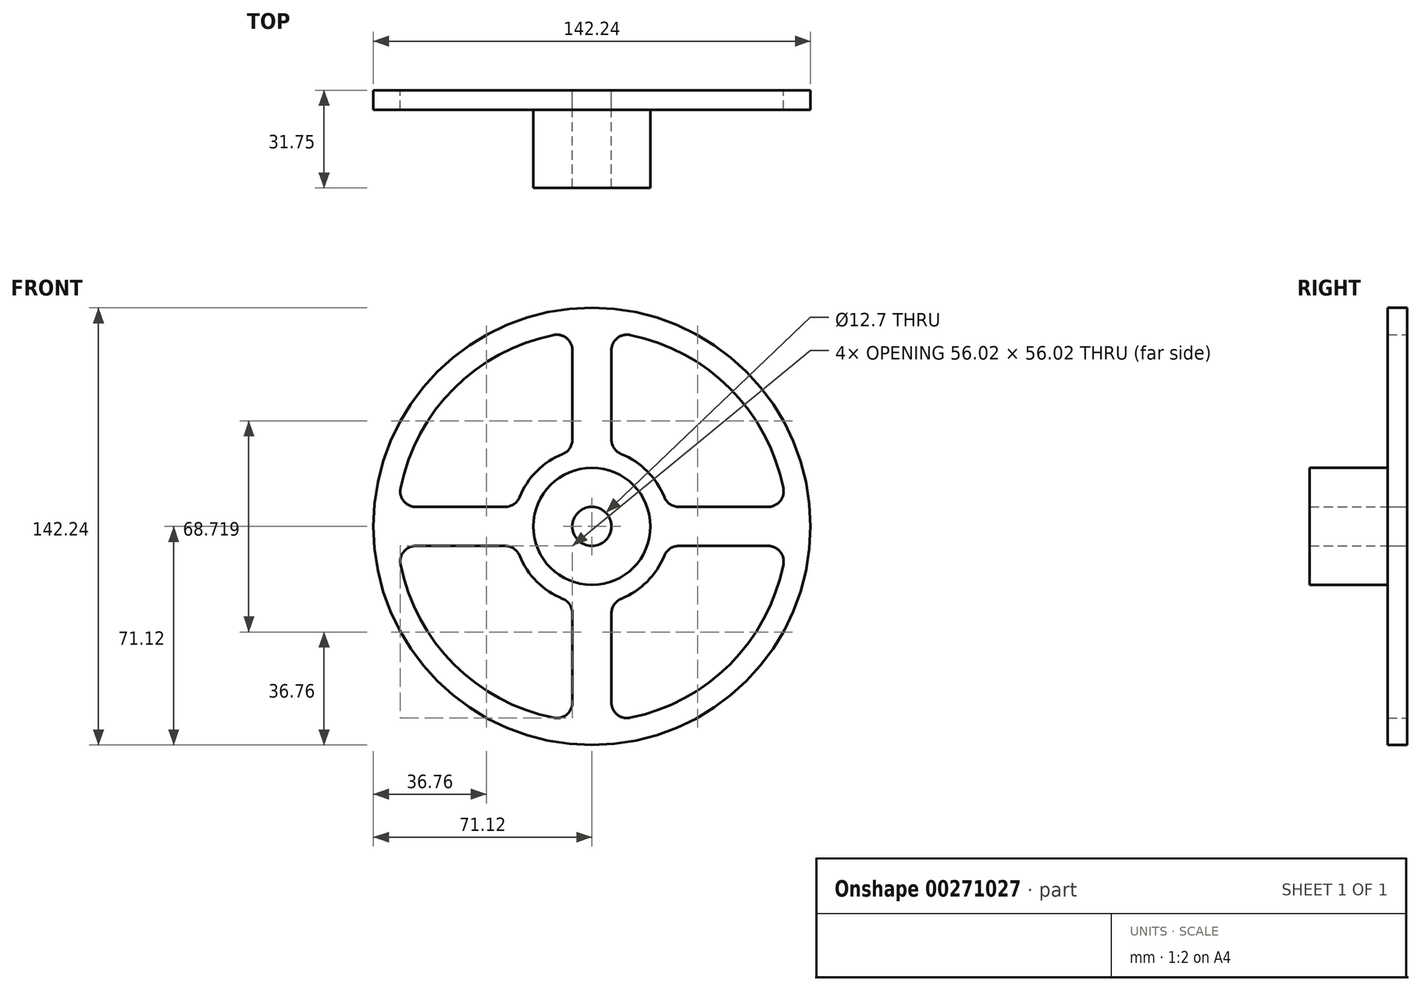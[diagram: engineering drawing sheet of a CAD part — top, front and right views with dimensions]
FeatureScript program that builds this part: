
annotation { "Feature Type Name" : "Feature", "Feature Type Description" : "" }
export const myFeature = defineFeature(function(context is Context, id is Id, definition is map)
    precondition{}
    {
        {
            var Q0;
            Q0=qCreatedBy(makeId("Front.planeOp"),FACE);
            var sketch = newSketch(context, id + "F0", { "sketchPlane" : qUnion([Q0])});
            skCircle(sketch, "E0", {"center": v(0, 0) * mm, "radius": 71.12 * mm});
            skArc(sketch, "E1", {"start": v(-9.52, 23.55) * mm, "mid": v(-17.96, 17.96) * mm, "end": v(-23.55, 9.52) * mm});
            skArc(sketch, "E2", {"start": v(-12.42, 62.27) * mm, "mid": v(-44.9, 44.9) * mm, "end": v(-62.27, 12.42) * mm});
            skLineSegment(sketch, "E3", {"start": v(0, 91.56) * mm, "end": v(0, -89.65) * mm, "construction": true});
            skLineSegment(sketch, "E4", {"start": v(129.78, 0) * mm, "end": v(-145.52, 0) * mm, "construction": true});
            skLineSegment(sketch, "E5", {"start": v(-6.35, 57.3) * mm, "end": v(-6.35, 28.26) * mm});
            skLineSegment(sketch, "E6", {"start": v(6.35, 57.3) * mm, "end": v(6.35, 28.26) * mm});
            skLineSegment(sketch, "E7", {"start": v(-57.3, 6.35) * mm, "end": v(-28.26, 6.35) * mm});
            skLineSegment(sketch, "E8", {"start": v(-57.3, -6.35) * mm, "end": v(-28.26, -6.35) * mm});
            skLineSegment(sketch, "E9", {"start": v(-6.35, -28.26) * mm, "end": v(-6.35, -57.3) * mm});
            skLineSegment(sketch, "E10", {"start": v(6.35, -28.26) * mm, "end": v(6.35, -57.3) * mm});
            skLineSegment(sketch, "E11", {"start": v(28.26, 6.35) * mm, "end": v(57.3, 6.35) * mm});
            skLineSegment(sketch, "E12", {"start": v(28.26, -6.35) * mm, "end": v(57.3, -6.35) * mm});
            skArc(sketch, "E13.trimOffspring", {"start": v(23.55, 9.52) * mm, "mid": v(17.96, 17.96) * mm, "end": v(9.53, 23.55) * mm});
            skArc(sketch, "E14.trimOffspring", {"start": v(9.53, -23.55) * mm, "mid": v(17.96, -17.96) * mm, "end": v(23.55, -9.53) * mm});
            skArc(sketch, "E15.trimOffspring", {"start": v(-23.55, -9.53) * mm, "mid": v(-17.96, -17.96) * mm, "end": v(-9.52, -23.55) * mm});
            skPoint(sketch, "E16.visualSharp", {"position": v(-6.35, 63.18) * mm});
            skArc(sketch, "E16.filletArc", {"start": v(-6.35, 57.3) * mm, "mid": v(-8.2, 61.22) * mm, "end": v(-12.42, 62.27) * mm});
            skPoint(sketch, "E17.visualSharp", {"position": v(6.35, 63.18) * mm});
            skArc(sketch, "E17.filletArc", {"start": v(12.42, 62.27) * mm, "mid": v(8.2, 61.22) * mm, "end": v(6.35, 57.3) * mm});
            skArc(sketch, "E18.trimOffspring", {"start": v(-62.27, -12.42) * mm, "mid": v(-44.9, -44.9) * mm, "end": v(-12.42, -62.27) * mm});
            skArc(sketch, "E19.trimOffspring", {"start": v(62.27, 12.42) * mm, "mid": v(44.9, 44.9) * mm, "end": v(12.42, 62.27) * mm});
            skPoint(sketch, "E20.visualSharp", {"position": v(-63.18, 6.35) * mm});
            skArc(sketch, "E20.filletArc", {"start": v(-62.27, 12.42) * mm, "mid": v(-61.22, 8.2) * mm, "end": v(-57.3, 6.35) * mm});
            skPoint(sketch, "E21.visualSharp", {"position": v(-63.18, -6.35) * mm});
            skArc(sketch, "E21.filletArc", {"start": v(-57.3, -6.35) * mm, "mid": v(-61.22, -8.2) * mm, "end": v(-62.27, -12.42) * mm});
            skPoint(sketch, "E22.visualSharp", {"position": v(63.18, 6.35) * mm});
            skArc(sketch, "E22.filletArc", {"start": v(57.3, 6.35) * mm, "mid": v(61.22, 8.2) * mm, "end": v(62.27, 12.42) * mm});
            skPoint(sketch, "E23.visualSharp", {"position": v(63.18, -6.35) * mm});
            skArc(sketch, "E23.filletArc", {"start": v(62.27, -12.42) * mm, "mid": v(61.22, -8.2) * mm, "end": v(57.3, -6.35) * mm});
            skArc(sketch, "E24.trimOffspring", {"start": v(12.42, -62.27) * mm, "mid": v(44.9, -44.9) * mm, "end": v(62.27, -12.42) * mm});
            skPoint(sketch, "E25.visualSharp", {"position": v(-6.35, -63.18) * mm});
            skArc(sketch, "E25.filletArc", {"start": v(-12.42, -62.27) * mm, "mid": v(-8.2, -61.22) * mm, "end": v(-6.35, -57.3) * mm});
            skPoint(sketch, "E26.visualSharp", {"position": v(6.35, -63.18) * mm});
            skArc(sketch, "E26.filletArc", {"start": v(6.35, -57.3) * mm, "mid": v(8.2, -61.22) * mm, "end": v(12.42, -62.27) * mm});
            skPoint(sketch, "E27.visualSharp", {"position": v(-6.35, -24.6) * mm});
            skArc(sketch, "E27.filletArc", {"start": v(-6.35, -28.26) * mm, "mid": v(-7.22, -25.42) * mm, "end": v(-9.52, -23.55) * mm});
            skPoint(sketch, "E28.visualSharp", {"position": v(-24.6, -6.35) * mm});
            skArc(sketch, "E28.filletArc", {"start": v(-23.55, -9.53) * mm, "mid": v(-25.42, -7.22) * mm, "end": v(-28.26, -6.35) * mm});
            skPoint(sketch, "E29.visualSharp", {"position": v(6.35, -24.6) * mm});
            skArc(sketch, "E29.filletArc", {"start": v(9.53, -23.55) * mm, "mid": v(7.22, -25.42) * mm, "end": v(6.35, -28.26) * mm});
            skPoint(sketch, "E30.visualSharp", {"position": v(24.6, -6.35) * mm});
            skArc(sketch, "E30.filletArc", {"start": v(28.26, -6.35) * mm, "mid": v(25.42, -7.22) * mm, "end": v(23.55, -9.53) * mm});
            skPoint(sketch, "E31.visualSharp", {"position": v(24.6, 6.35) * mm});
            skArc(sketch, "E31.filletArc", {"start": v(23.55, 9.52) * mm, "mid": v(25.42, 7.22) * mm, "end": v(28.26, 6.35) * mm});
            skPoint(sketch, "E32.visualSharp", {"position": v(6.35, 24.6) * mm});
            skArc(sketch, "E32.filletArc", {"start": v(6.35, 28.26) * mm, "mid": v(7.22, 25.42) * mm, "end": v(9.53, 23.55) * mm});
            skPoint(sketch, "E33.visualSharp", {"position": v(-6.35, 24.6) * mm});
            skArc(sketch, "E33.filletArc", {"start": v(-9.52, 23.55) * mm, "mid": v(-7.22, 25.42) * mm, "end": v(-6.35, 28.26) * mm});
            skPoint(sketch, "E34.visualSharp", {"position": v(-24.6, 6.35) * mm});
            skArc(sketch, "E34.filletArc", {"start": v(-28.26, 6.35) * mm, "mid": v(-25.42, 7.22) * mm, "end": v(-23.55, 9.52) * mm});
            skSolve(sketch);
        }
        {
            var Q0;
            Q0 = qSketchRegion(id + "F0", true);
            extrude(context, id + "F1", {"entities" : qUnion([Q0]), "depth" : 6.35 * mm});
        }
        {
            var Q0;
            Q0=makeQuery(id+"F1.opExtrude","CAP_FACE",FACE,{"disambiguationData":[OSD([sQuery(id+"F0.wireOp",EDGE,"E0"),sQuery(id+"F0.wireOp",EDGE,"E1"),sQuery(id+"F0.wireOp",EDGE,"E2"),sQuery(id+"F0.wireOp",EDGE,"E5"),sQuery(id+"F0.wireOp",EDGE,"E6"),sQuery(id+"F0.wireOp",EDGE,"E7"),sQuery(id+"F0.wireOp",EDGE,"E8"),sQuery(id+"F0.wireOp",EDGE,"E9"),sQuery(id+"F0.wireOp",EDGE,"E10"),sQuery(id+"F0.wireOp",EDGE,"E11"),sQuery(id+"F0.wireOp",EDGE,"E12"),sQuery(id+"F0.wireOp",EDGE,"E13.trimOffspring"),sQuery(id+"F0.wireOp",EDGE,"E14.trimOffspring"),sQuery(id+"F0.wireOp",EDGE,"E15.trimOffspring"),sQuery(id+"F0.wireOp",EDGE,"E16.filletArc"),sQuery(id+"F0.wireOp",EDGE,"E17.filletArc"),sQuery(id+"F0.wireOp",EDGE,"E18.trimOffspring"),sQuery(id+"F0.wireOp",EDGE,"E19.trimOffspring"),sQuery(id+"F0.wireOp",EDGE,"E20.filletArc"),sQuery(id+"F0.wireOp",EDGE,"E21.filletArc"),sQuery(id+"F0.wireOp",EDGE,"E22.filletArc"),sQuery(id+"F0.wireOp",EDGE,"E23.filletArc"),sQuery(id+"F0.wireOp",EDGE,"E24.trimOffspring"),sQuery(id+"F0.wireOp",EDGE,"E25.filletArc"),sQuery(id+"F0.wireOp",EDGE,"E26.filletArc"),sQuery(id+"F0.wireOp",EDGE,"E27.filletArc"),sQuery(id+"F0.wireOp",EDGE,"E28.filletArc"),sQuery(id+"F0.wireOp",EDGE,"E29.filletArc"),sQuery(id+"F0.wireOp",EDGE,"E30.filletArc"),sQuery(id+"F0.wireOp",EDGE,"E31.filletArc"),sQuery(id+"F0.wireOp",EDGE,"E32.filletArc"),sQuery(id+"F0.wireOp",EDGE,"E33.filletArc"),sQuery(id+"F0.wireOp",EDGE,"E34.filletArc")])],"isStart":false});
            var sketch = newSketch(context, id + "F2", { "sketchPlane" : qUnion([Q0])});
            skCircle(sketch, "E35", {"center": v(0, 0) * mm, "radius": 19.05 * mm});
            skCircle(sketch, "E36", {"center": v(0, 0) * mm, "radius": 6.35 * mm});
            skSolve(sketch);
        }
        {
            var Q0;
            Q0 = qSketchRegion(id + "F2", true);
            extrude(context, id + "F3", {"entities" : qUnion([Q0]), "operationType" : NewBodyOperationType.ADD, "depth" : 25.4 * mm});
        }
        {
            var Q0;
            Q0=makeQuery(id+"F3.boolean.opBoolean","SPLIT",FACE,{"disambiguationData":[TD([makeQuery(id+"F3.opExtrude","SWEPT_FACE",FACE,{"disambiguationData":[OSD([sQuery(id+"F2.wireOp",EDGE,"E36")])]})])],"derivedFrom":makeQuery(id+"F1.opExtrude","CAP_FACE",FACE,{"disambiguationData":[OSD([sQuery(id+"F0.wireOp",EDGE,"E0"),sQuery(id+"F0.wireOp",EDGE,"E1"),sQuery(id+"F0.wireOp",EDGE,"E2"),sQuery(id+"F0.wireOp",EDGE,"E5"),sQuery(id+"F0.wireOp",EDGE,"E6"),sQuery(id+"F0.wireOp",EDGE,"E7"),sQuery(id+"F0.wireOp",EDGE,"E8"),sQuery(id+"F0.wireOp",EDGE,"E9"),sQuery(id+"F0.wireOp",EDGE,"E10"),sQuery(id+"F0.wireOp",EDGE,"E11"),sQuery(id+"F0.wireOp",EDGE,"E12"),sQuery(id+"F0.wireOp",EDGE,"E13.trimOffspring"),sQuery(id+"F0.wireOp",EDGE,"E14.trimOffspring"),sQuery(id+"F0.wireOp",EDGE,"E15.trimOffspring"),sQuery(id+"F0.wireOp",EDGE,"E16.filletArc"),sQuery(id+"F0.wireOp",EDGE,"E17.filletArc"),sQuery(id+"F0.wireOp",EDGE,"E18.trimOffspring"),sQuery(id+"F0.wireOp",EDGE,"E19.trimOffspring"),sQuery(id+"F0.wireOp",EDGE,"E20.filletArc"),sQuery(id+"F0.wireOp",EDGE,"E21.filletArc"),sQuery(id+"F0.wireOp",EDGE,"E22.filletArc"),sQuery(id+"F0.wireOp",EDGE,"E23.filletArc"),sQuery(id+"F0.wireOp",EDGE,"E24.trimOffspring"),sQuery(id+"F0.wireOp",EDGE,"E25.filletArc"),sQuery(id+"F0.wireOp",EDGE,"E26.filletArc"),sQuery(id+"F0.wireOp",EDGE,"E27.filletArc"),sQuery(id+"F0.wireOp",EDGE,"E28.filletArc"),sQuery(id+"F0.wireOp",EDGE,"E29.filletArc"),sQuery(id+"F0.wireOp",EDGE,"E30.filletArc"),sQuery(id+"F0.wireOp",EDGE,"E31.filletArc"),sQuery(id+"F0.wireOp",EDGE,"E32.filletArc"),sQuery(id+"F0.wireOp",EDGE,"E33.filletArc"),sQuery(id+"F0.wireOp",EDGE,"E34.filletArc")])],"isStart":false})});
            extrude(context, id + "F4", {"entities" : qUnion([Q0]), "operationType" : NewBodyOperationType.REMOVE, "endBound" : BoundingType.THROUGH_ALL, "oppositeDirection" : true, "depth" : 25.4 * mm});
        }
    });
